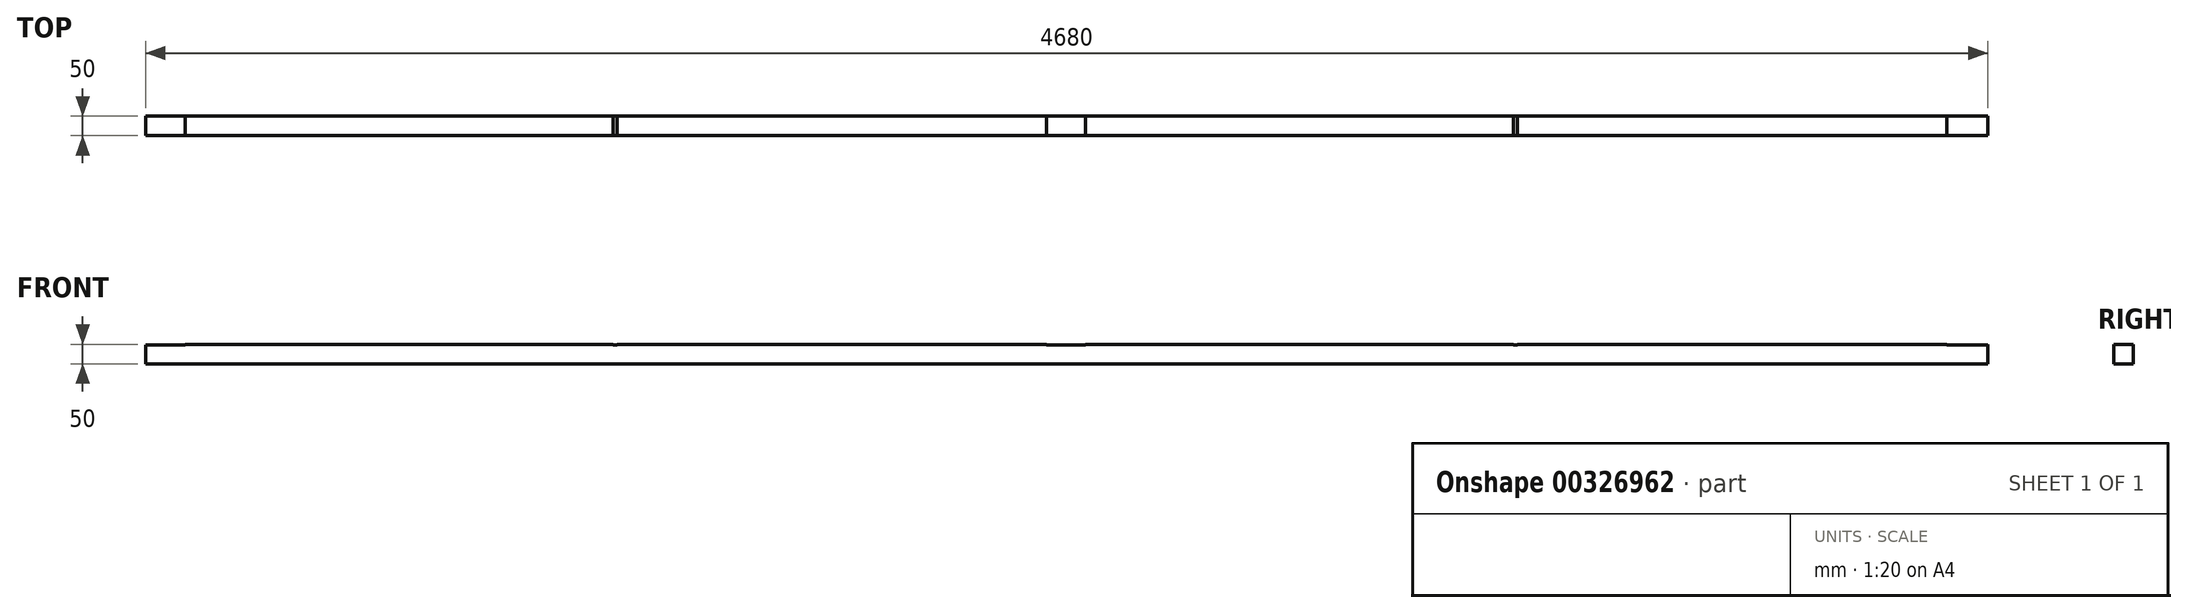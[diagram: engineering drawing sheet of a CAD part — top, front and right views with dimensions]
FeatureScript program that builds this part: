
annotation { "Feature Type Name" : "Feature", "Feature Type Description" : "" }
export const myFeature = defineFeature(function(context is Context, id is Id, definition is map)
    precondition{}
    {
        {
            var Q0;
            Q0=qCreatedBy(makeId("Top.planeOp"),FACE);
            var sketch = newSketch(context, id + "F0", { "sketchPlane" : qUnion([Q0])});
            skLineSegment(sketch, "E0", {"start": v(0, 0) * mm, "end": v(4680, 0) * mm});
            skLineSegment(sketch, "E1", {"start": v(4680, 0) * mm, "end": v(4680, 50) * mm});
            skLineSegment(sketch, "E2", {"start": v(4680, 50) * mm, "end": v(0, 50) * mm});
            skLineSegment(sketch, "E3", {"start": v(0, 50) * mm, "end": v(0, 0) * mm});
            skSolve(sketch);
        }
        {
            var Q0;
            Q0 = qSketchRegion(id + "F0", true);
            extrude(context, id + "F1", {"entities" : qUnion([Q0]), "depth" : 50 * mm});
        }
        {
            var Q0;
            Q0=makeQuery(id+"F1.opExtrude","CAP_FACE",FACE,{"disambiguationData":[OSD([sQuery(id+"F0.wireOp",EDGE,"E0"),sQuery(id+"F0.wireOp",EDGE,"E1"),sQuery(id+"F0.wireOp",EDGE,"E2"),sQuery(id+"F0.wireOp",EDGE,"E3")])],"isStart":false});
            var sketch = newSketch(context, id + "F2", { "sketchPlane" : qUnion([Q0])});
            skLineSegment(sketch, "E4.bottom", {"start": v(0, 50) * mm, "end": v(100, 50) * mm});
            skLineSegment(sketch, "E4.top", {"start": v(0, 0) * mm, "end": v(100, 0) * mm});
            skLineSegment(sketch, "E4.left", {"start": v(0, 50) * mm, "end": v(0, 0) * mm});
            skLineSegment(sketch, "E4.right", {"start": v(100, 50) * mm, "end": v(100, 0) * mm});
            skSolve(sketch);
        }
        {
            var Q0;
            Q0 = qSketchRegion(id + "F2", true);
            extrude(context, id + "F3", {"entities" : qUnion([Q0]), "operationType" : NewBodyOperationType.REMOVE, "oppositeDirection" : true, "depth" : 2 * mm});
        }
        {
            var Q0;
            Q0=makeQuery(id+"F1.opExtrude","CAP_FACE",FACE,{"disambiguationData":[OSD([sQuery(id+"F0.wireOp",EDGE,"E0"),sQuery(id+"F0.wireOp",EDGE,"E1"),sQuery(id+"F0.wireOp",EDGE,"E2"),sQuery(id+"F0.wireOp",EDGE,"E3")])],"isStart":false});
            var sketch = newSketch(context, id + "F4", { "sketchPlane" : qUnion([Q0])});
            skLineSegment(sketch, "E5.bottom", {"start": v(100, 50) * mm, "end": v(1190, 50) * mm});
            skLineSegment(sketch, "E5.top", {"start": v(100, 0) * mm, "end": v(1190, 0) * mm});
            skLineSegment(sketch, "E5.left", {"start": v(100, 50) * mm, "end": v(100, 0) * mm});
            skLineSegment(sketch, "E5.right", {"start": v(1190, 50) * mm, "end": v(1190, 0) * mm});
            skSolve(sketch);
        }
        {
            var Q0;
            {var subQ0=sQuery(id+"F4.wireOp",EDGE,"E5.right");Q0=makeQuery(id+"F4.imprint","IMPRINT",FACE,{"disambiguationData":[TD([[makeQuery(id+"F4.imprint","IMPRINT",EDGE,{"derivedFrom":subQ0}),1.0]])]});}
            var sketch = newSketch(context, id + "F5", { "sketchPlane" : qUnion([Q0])});
            skLineSegment(sketch, "E6.bottom", {"start": v(1187.84, 55.15) * mm, "end": v(1197.84, 55.15) * mm});
            skLineSegment(sketch, "E6.top", {"start": v(1187.84, 0) * mm, "end": v(1197.84, 0) * mm});
            skLineSegment(sketch, "E6.left", {"start": v(1187.84, 55.15) * mm, "end": v(1187.84, 0) * mm});
            skLineSegment(sketch, "E6.right", {"start": v(1197.84, 55.15) * mm, "end": v(1197.84, 0) * mm});
            skSolve(sketch);
        }
        {
            var Q0;
            Q0 = qSketchRegion(id + "F5", true);
            extrude(context, id + "F6", {"entities" : qUnion([Q0]), "operationType" : NewBodyOperationType.REMOVE, "oppositeDirection" : true, "depth" : 2 * mm});
        }
        {
            var Q0;
            {var subQ0=sQuery(id+"F4.wireOp",EDGE,"E5.right");Q0=makeQuery(id+"F4.imprint","IMPRINT",FACE,{"disambiguationData":[TD([[makeQuery(id+"F4.imprint","IMPRINT",EDGE,{"derivedFrom":subQ0}),1.0]])]});}
            var sketch = newSketch(context, id + "F7", { "sketchPlane" : qUnion([Q0])});
            skLineSegment(sketch, "E7.bottom", {"start": v(2288, 50.6) * mm, "end": v(2388, 50.6) * mm});
            skLineSegment(sketch, "E7.top", {"start": v(2288, 0) * mm, "end": v(2388, 0) * mm});
            skLineSegment(sketch, "E7.left", {"start": v(2288, 50.6) * mm, "end": v(2288, 0) * mm});
            skLineSegment(sketch, "E7.right", {"start": v(2388, 50.6) * mm, "end": v(2388, 0) * mm});
            skSolve(sketch);
        }
        {
            var Q0;
            Q0 = qSketchRegion(id + "F7", true);
            extrude(context, id + "F8", {"entities" : qUnion([Q0]), "operationType" : NewBodyOperationType.REMOVE, "oppositeDirection" : true, "depth" : 2 * mm});
        }
        {
            var Q0;
            {var subQ0=sQuery(id+"F4.wireOp",EDGE,"E5.right");Q0=makeQuery(id+"F4.imprint","IMPRINT",FACE,{"disambiguationData":[TD([[makeQuery(id+"F4.imprint","IMPRINT",EDGE,{"derivedFrom":subQ0}),1.0]])]});}
            var sketch = newSketch(context, id + "F9", { "sketchPlane" : qUnion([Q0])});
            skLineSegment(sketch, "E8.bottom", {"start": v(3474.99, 53.39) * mm, "end": v(3484.99, 53.39) * mm});
            skLineSegment(sketch, "E8.top", {"start": v(3474.99, 0) * mm, "end": v(3484.99, 0) * mm});
            skLineSegment(sketch, "E8.left", {"start": v(3474.99, 53.39) * mm, "end": v(3474.99, 0) * mm});
            skLineSegment(sketch, "E8.right", {"start": v(3484.99, 53.39) * mm, "end": v(3484.99, 0) * mm});
            skSolve(sketch);
        }
        {
            var Q0;
            Q0 = qSketchRegion(id + "F9", true);
            extrude(context, id + "F10", {"entities" : qUnion([Q0]), "operationType" : NewBodyOperationType.REMOVE, "oppositeDirection" : true, "depth" : 2 * mm});
        }
        {
            var Q0;
            {var subQ0=sQuery(id+"F4.wireOp",EDGE,"E5.right");Q0=makeQuery(id+"F4.imprint","IMPRINT",FACE,{"disambiguationData":[TD([[makeQuery(id+"F4.imprint","IMPRINT",EDGE,{"derivedFrom":subQ0}),1.0]])]});}
            var sketch = newSketch(context, id + "F11", { "sketchPlane" : qUnion([Q0])});
            skLineSegment(sketch, "E9.bottom", {"start": v(4575.25, 51.4) * mm, "end": v(4679.48, 51.4) * mm});
            skLineSegment(sketch, "E9.top", {"start": v(4575.25, 0) * mm, "end": v(4679.48, 0) * mm});
            skLineSegment(sketch, "E9.left", {"start": v(4575.25, 51.4) * mm, "end": v(4575.25, 0) * mm});
            skLineSegment(sketch, "E9.right", {"start": v(4679.48, 51.4) * mm, "end": v(4679.48, 0) * mm});
            skSolve(sketch);
        }
        {
            var Q0;
            Q0 = qSketchRegion(id + "F11", true);
            extrude(context, id + "F12", {"entities" : qUnion([Q0]), "operationType" : NewBodyOperationType.REMOVE, "oppositeDirection" : true, "depth" : 2 * mm});
        }
    });
